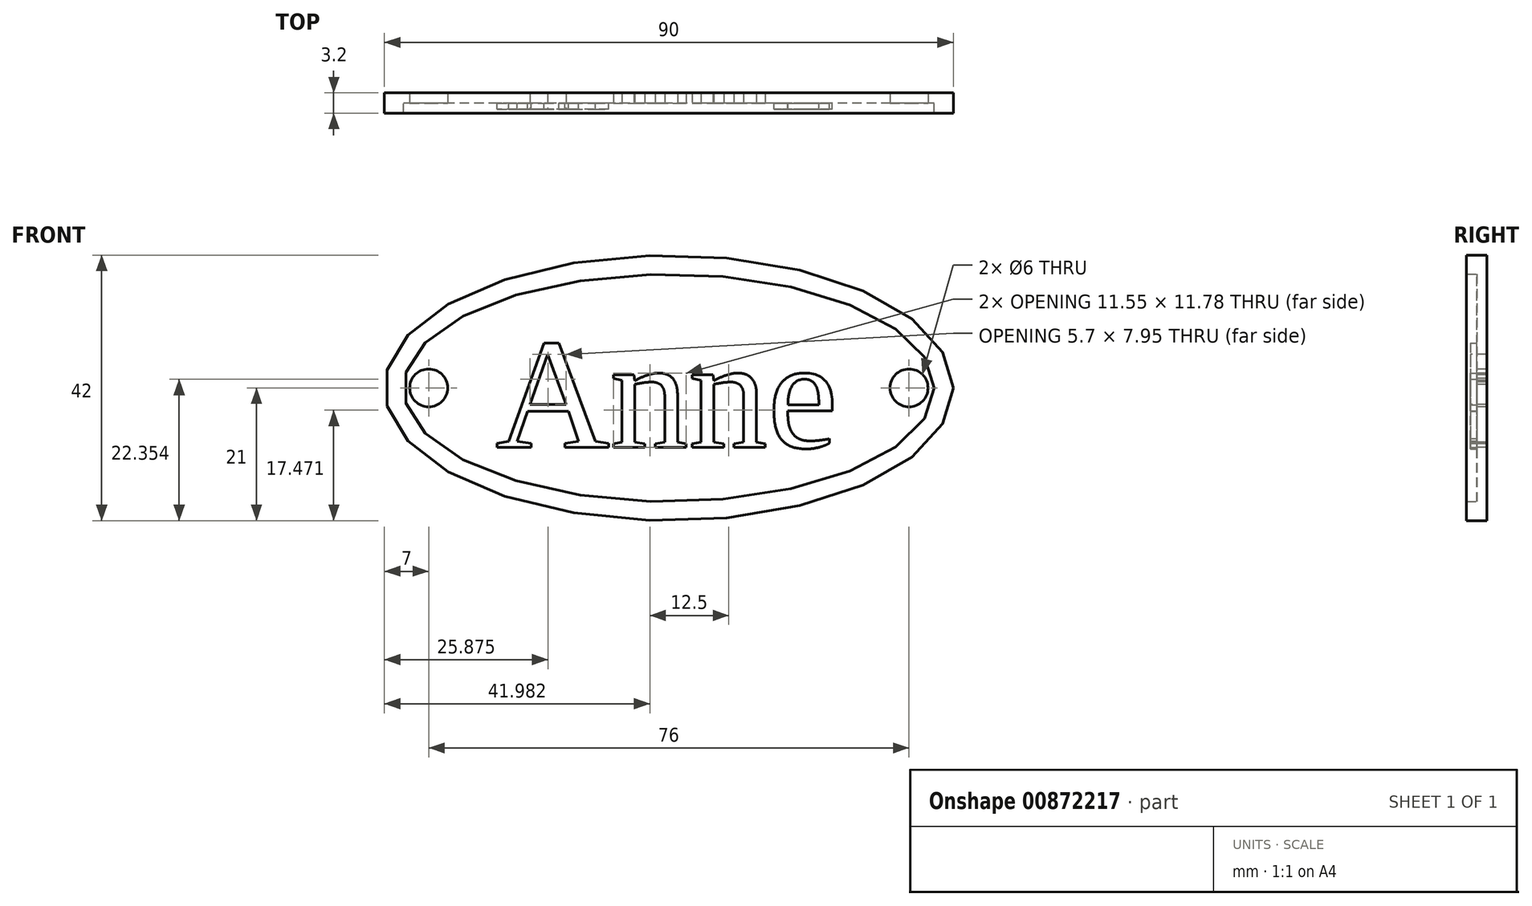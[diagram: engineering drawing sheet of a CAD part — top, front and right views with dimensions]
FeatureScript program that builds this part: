
annotation { "Feature Type Name" : "Feature", "Feature Type Description" : "" }
export const myFeature = defineFeature(function(context is Context, id is Id, definition is map)
    precondition{}
    {
        {
            var Q0;
            Q0=qCreatedBy(makeId("Front.planeOp"),FACE);
            var sketch = newSketch(context, id + "F0", { "sketchPlane" : qUnion([Q0])});
            skEllipse(sketch, "E0", {"center": v(0, 0) * mm, "majorRadius": 42 * mm, "minorRadius": 18 * mm, "majorAxis": v(1, 0)});
            skEllipse(sketch, "E1", {"center": v(0, 0) * mm, "majorRadius": 45 * mm, "minorRadius": 21 * mm, "majorAxis": v(1, 0)});
            skLineSegment(sketch, "E2", {"start": v(-81.12, 0) * mm, "end": v(85, 0) * mm, "construction": true});
            skPoint(sketch, "E2.startSnap0", {"position": v(-45, 0) * mm});
            skPoint(sketch, "E2.endSnap0", {"position": v(45, 0) * mm});
            skCircle(sketch, "E3", {"center": v(-38, 0) * mm, "radius": 3 * mm});
            skCircle(sketch, "E4", {"center": v(38, 0) * mm, "radius": 3 * mm});
            skText(sketch, "E5", { "text": "Anne", "fontName": "Tinos-Regular.ttf"});
            const initialGuessF0  = {"E5": [-0.02742, -0.00942, 1, 0, 0.018]};
            skSetInitialGuess(sketch, initialGuessF0);
            skSolve(sketch);
        }
        {
            var Q0;
            Q0=makeQuery(id+"F0.imprint","IMPRINT",FACE,{"disambiguationData":[TD([[makeQuery(id+"F0.imprint","IMPRINT",EDGE,{"derivedFrom":sQuery(id+"F0.wireOp",EDGE,"E0")}),1.0]])]});
            var Q1;
            Q1=makeQuery(id+"F0.imprint","IMPRINT",FACE,{"disambiguationData":[TD([[makeQuery(id+"F0.imprint","IMPRINT",EDGE,{"derivedFrom":sQuery(id+"F0.wireOp",EDGE,"E5.sketch_text.stroke-0")}),-1.0]])]});
            var Q2;
            Q2=makeQuery(id+"F0.imprint","IMPRINT",FACE,{"disambiguationData":[TD([[makeQuery(id+"F0.imprint","IMPRINT",EDGE,{"derivedFrom":sQuery(id+"F0.wireOp",EDGE,"E5.sketch_text.stroke-28")}),-1.0]])]});
            var Q3;
            Q3=makeQuery(id+"F0.imprint","IMPRINT",FACE,{"disambiguationData":[TD([[makeQuery(id+"F0.imprint","IMPRINT",EDGE,{"derivedFrom":sQuery(id+"F0.wireOp",EDGE,"E5.sketch_text.stroke-44")}),1.0]])]});
            var Q4;
            Q4=makeQuery(id+"F0.imprint","IMPRINT",FACE,{"disambiguationData":[TD([[makeQuery(id+"F0.imprint","IMPRINT",EDGE,{"derivedFrom":sQuery(id+"F0.wireOp",EDGE,"E0")}),-1.0]])]});
            var Q5;
            Q5=makeQuery(id+"F0.imprint","IMPRINT",FACE,{"disambiguationData":[TD([[makeQuery(id+"F0.imprint","IMPRINT",EDGE,{"derivedFrom":sQuery(id+"F0.wireOp",EDGE,"E5.sketch_text.stroke-59")}),-1.0]])]});
            var Q6;
            Q6=makeQuery(id+"F0.imprint","IMPRINT",FACE,{"disambiguationData":[TD([[makeQuery(id+"F0.imprint","IMPRINT",EDGE,{"derivedFrom":sQuery(id+"F0.wireOp",EDGE,"E5.sketch_text.stroke-69")}),-1.0]])]});
            var Q7;
            Q7=makeQuery(id+"F0.imprint","IMPRINT",FACE,{"disambiguationData":[TD([[makeQuery(id+"F0.imprint","IMPRINT",EDGE,{"derivedFrom":sQuery(id+"F0.wireOp",EDGE,"E5.sketch_text.stroke-85")}),1.0]])]});
            var Q8;
            Q8=makeQuery(id+"F0.imprint","IMPRINT",FACE,{"disambiguationData":[TD([[makeQuery(id+"F0.imprint","IMPRINT",EDGE,{"derivedFrom":sQuery(id+"F0.wireOp",EDGE,"E5.sketch_text.stroke-49")}),-1.0]])]});
            var Q9;
            Q9=makeQuery(id+"F0.imprint","IMPRINT",FACE,{"disambiguationData":[TD([[makeQuery(id+"F0.imprint","IMPRINT",EDGE,{"derivedFrom":sQuery(id+"F0.wireOp",EDGE,"E5.sketch_text.stroke-39")}),1.0]])]});
            var Q10;
            Q10=makeQuery(id+"F0.imprint","IMPRINT",FACE,{"disambiguationData":[TD([[makeQuery(id+"F0.imprint","IMPRINT",EDGE,{"derivedFrom":sQuery(id+"F0.wireOp",EDGE,"E5.sketch_text.stroke-72")}),-1.0]])]});
            var Q11;
            Q11=makeQuery(id+"F0.imprint","IMPRINT",FACE,{"disambiguationData":[TD([[makeQuery(id+"F0.imprint","IMPRINT",EDGE,{"derivedFrom":sQuery(id+"F0.wireOp",EDGE,"E5.sketch_text.stroke-74")}),-1.0]])]});
            var Q12;
            Q12=makeQuery(id+"F0.imprint","IMPRINT",FACE,{"disambiguationData":[TD([[makeQuery(id+"F0.imprint","IMPRINT",EDGE,{"derivedFrom":sQuery(id+"F0.wireOp",EDGE,"E5.sketch_text.stroke-68")}),1.0]])]});
            var Q13;
            Q13=makeQuery(id+"F0.imprint","IMPRINT",FACE,{"disambiguationData":[TD([[makeQuery(id+"F0.imprint","IMPRINT",EDGE,{"derivedFrom":sQuery(id+"F0.wireOp",EDGE,"E5.sketch_text.stroke-46")}),1.0]])]});
            extrude(context, id + "F1", {"entities" : qUnion([Q0, Q1, Q2, Q3, Q4, Q5, Q6, Q7, Q8, Q9, Q10, Q11, Q12, Q13]), "oppositeDirection" : true, "depth" : 1.6 * mm, "offsetDistance" : 25 * mm});
        }
        {
            var Q0;
            Q0=makeQuery(id+"F0.imprint","IMPRINT",FACE,{"disambiguationData":[TD([[makeQuery(id+"F0.imprint","IMPRINT",EDGE,{"derivedFrom":sQuery(id+"F0.wireOp",EDGE,"E0")}),-1.0]])]});
            extrude(context, id + "F2", {"entities" : qUnion([Q0]), "operationType" : NewBodyOperationType.ADD, "depth" : 1.6 * mm, "offsetDistance" : 25 * mm});
        }
        {
            var Q0;
            Q0=makeQuery(id+"F0.imprint","IMPRINT",FACE,{"disambiguationData":[TD([[makeQuery(id+"F0.imprint","IMPRINT",EDGE,{"derivedFrom":sQuery(id+"F0.wireOp",EDGE,"E5.sketch_text.stroke-0")}),-1.0]])]});
            var Q1;
            Q1=makeQuery(id+"F0.imprint","IMPRINT",FACE,{"disambiguationData":[TD([[makeQuery(id+"F0.imprint","IMPRINT",EDGE,{"derivedFrom":sQuery(id+"F0.wireOp",EDGE,"E5.sketch_text.stroke-28")}),-1.0]])]});
            var Q2;
            Q2=makeQuery(id+"F0.imprint","IMPRINT",FACE,{"disambiguationData":[TD([[makeQuery(id+"F0.imprint","IMPRINT",EDGE,{"derivedFrom":sQuery(id+"F0.wireOp",EDGE,"E5.sketch_text.stroke-49")}),-1.0]])]});
            var Q3;
            Q3=makeQuery(id+"F0.imprint","IMPRINT",FACE,{"disambiguationData":[TD([[makeQuery(id+"F0.imprint","IMPRINT",EDGE,{"derivedFrom":sQuery(id+"F0.wireOp",EDGE,"E5.sketch_text.stroke-59")}),-1.0]])]});
            var Q4;
            Q4=makeQuery(id+"F0.imprint","IMPRINT",FACE,{"disambiguationData":[TD([[makeQuery(id+"F0.imprint","IMPRINT",EDGE,{"derivedFrom":sQuery(id+"F0.wireOp",EDGE,"E5.sketch_text.stroke-69")}),-1.0]])]});
            var Q5;
            Q5=makeQuery(id+"F0.imprint","IMPRINT",FACE,{"disambiguationData":[TD([[makeQuery(id+"F0.imprint","IMPRINT",EDGE,{"derivedFrom":sQuery(id+"F0.wireOp",EDGE,"E5.sketch_text.stroke-72")}),-1.0]])]});
            var Q6;
            Q6=makeQuery(id+"F0.imprint","IMPRINT",FACE,{"disambiguationData":[TD([[makeQuery(id+"F0.imprint","IMPRINT",EDGE,{"derivedFrom":sQuery(id+"F0.wireOp",EDGE,"E5.sketch_text.stroke-74")}),-1.0]])]});
            extrude(context, id + "F3", {"entities" : qUnion([Q0, Q1, Q2, Q3, Q4, Q5, Q6]), "operationType" : NewBodyOperationType.ADD, "depth" : 1 * mm, "offsetDistance" : 25 * mm});
        }
    });
